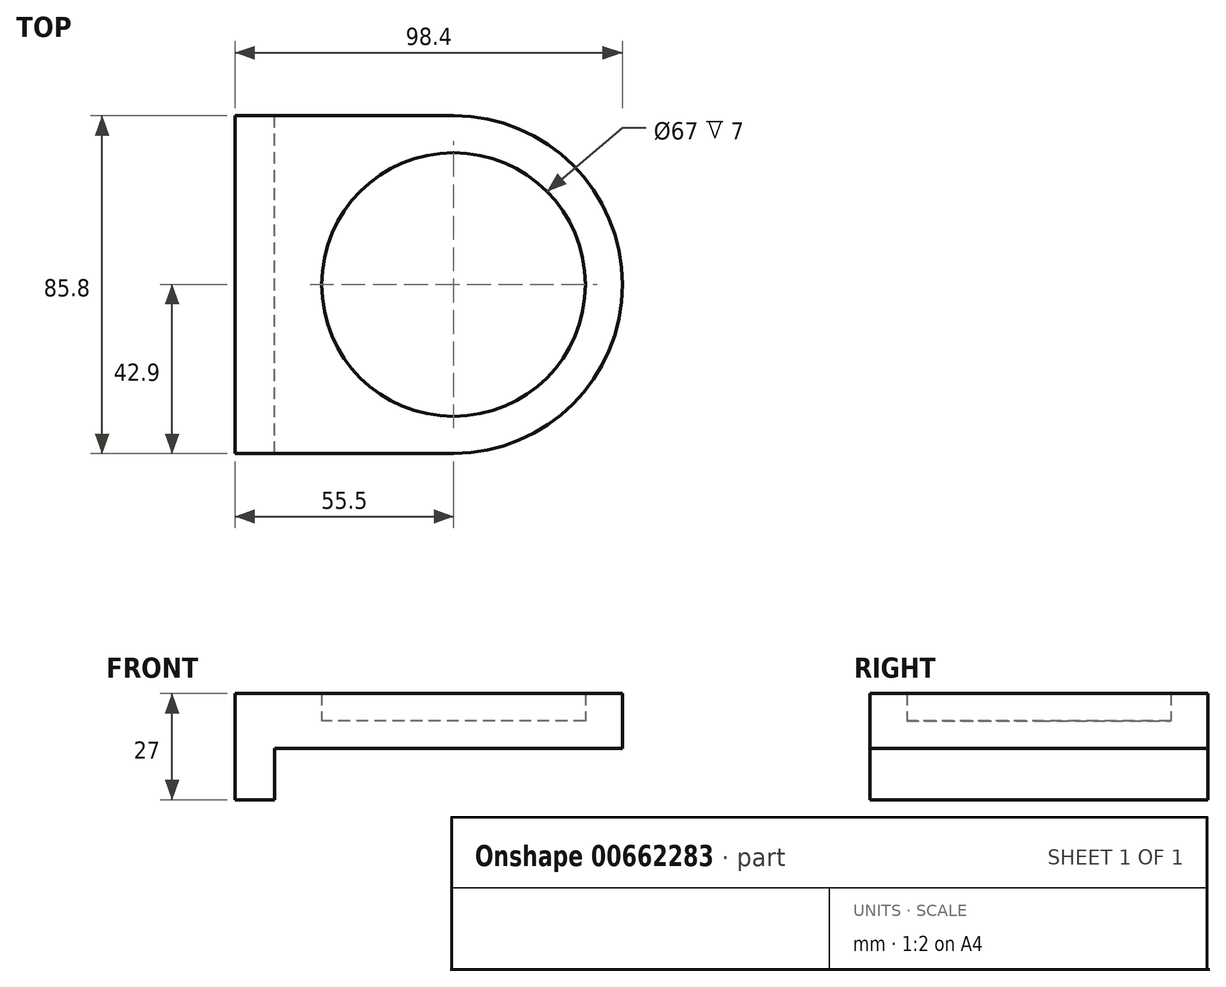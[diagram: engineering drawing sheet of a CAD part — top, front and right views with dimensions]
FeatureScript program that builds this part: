
annotation { "Feature Type Name" : "Feature", "Feature Type Description" : "" }
export const myFeature = defineFeature(function(context is Context, id is Id, definition is map)
    precondition{}
    {
        {
            var Q0;
            Q0=qCreatedBy(makeId("Top.planeOp"),FACE);
            var sketch = newSketch(context, id + "F0", { "sketchPlane" : qUnion([Q0])});
            skCircle(sketch, "E0", {"center": v(0, 0) * mm, "radius": 33.5 * mm});
            skCircle(sketch, "E1", {"center": v(0, 0) * mm, "radius": 42.9 * mm});
            skLineSegment(sketch, "E2", {"start": v(0, 42.9) * mm, "end": v(-55.5, 42.9) * mm});
            skLineSegment(sketch, "E3", {"start": v(-55.5, -42.9) * mm, "end": v(0, -42.9) * mm});
            skLineSegment(sketch, "E4", {"start": v(-55.5, 42.9) * mm, "end": v(-55.5, -42.9) * mm});
            skSolve(sketch);
        }
        {
            var Q0;
            {var subQ0=sQuery(id+"F0.wireOp",EDGE,"E3");Q0=makeQuery(id+"F0.imprint","IMPRINT",FACE,{"disambiguationData":[TD([[makeQuery(id+"F0.imprint","IMPRINT",EDGE,{"derivedFrom":subQ0}),1.0]])]});}
            var Q1;
            {var subQ0=sQuery(id+"F0.wireOp",EDGE,"E2");Q1=makeQuery(id+"F0.imprint","IMPRINT",FACE,{"disambiguationData":[TD([[makeQuery(id+"F0.imprint","IMPRINT",EDGE,{"derivedFrom":subQ0}),1.0]])]});}
            var Q2;
            Q2=makeQuery(id+"F0.imprint","IMPRINT",FACE,{"disambiguationData":[TD([[makeQuery(id+"F0.imprint","IMPRINT",EDGE,{"derivedFrom":sQuery(id+"F0.wireOp",EDGE,"E0")}),-1.0]])]});
            extrude(context, id + "F1", {"entities" : qUnion([Q0, Q1, Q2]), "depth" : 7 * mm, "offsetDistance" : 25.4 * mm});
        }
        {
            var Q0;
            Q0=makeQuery(id+"F1.opExtrude","CAP_FACE",FACE,{"disambiguationData":[OSD([sQuery(id+"F0.wireOp",EDGE,"E0"),sQuery(id+"F0.wireOp",EDGE,"E1"),sQuery(id+"F0.wireOp",EDGE,"E2"),sQuery(id+"F0.wireOp",EDGE,"B6yvLt6C-i46t-O52Y-Rehz-RWSLDy2yBdGn"),sQuery(id+"F0.wireOp",EDGE,"E3")])],"isStart":true});
            var sketch = newSketch(context, id + "F2", { "sketchPlane" : qUnion([Q0])});
            skArc(sketch, "E5", {"start": v(0, -42.9) * mm, "mid": v(42.9, 0) * mm, "end": v(0, 42.9) * mm});
            skLineSegment(sketch, "E6", {"start": v(-55.5, 42.9) * mm, "end": v(0, 42.9) * mm});
            skLineSegment(sketch, "E7", {"start": v(0, -42.9) * mm, "end": v(0, -42.9) * mm});
            skLineSegment(sketch, "E8", {"start": v(-55.5, 42.9) * mm, "end": v(-55.5, -42.9) * mm});
            skLineSegment(sketch, "E9", {"start": v(-55.5, -42.9) * mm, "end": v(0, -42.9) * mm});
            skSolve(sketch);
        }
        {
            var Q0;
            Q0 = qSketchRegion(id + "F2", true);
            extrude(context, id + "F3", {"entities" : qUnion([Q0]), "operationType" : NewBodyOperationType.ADD, "depth" : 7 * mm, "offsetDistance" : 25.4 * mm});
        }
        {
            var Q0;
            Q0=makeQuery(id+"F3.opExtrude","CAP_FACE",FACE,{"disambiguationData":[OSD([sQuery(id+"F2.wireOp",EDGE,"E5"),sQuery(id+"F2.wireOp",EDGE,"E6"),sQuery(id+"F2.wireOp",EDGE,"E8"),sQuery(id+"F2.wireOp",EDGE,"E9")])],"isStart":false});
            var sketch = newSketch(context, id + "F4", { "sketchPlane" : qUnion([Q0])});
            skLineSegment(sketch, "E10.bottom", {"start": v(-55.5, 42.9) * mm, "end": v(-45.5, 42.9) * mm});
            skLineSegment(sketch, "E10.top", {"start": v(-55.5, -42.9) * mm, "end": v(-45.5, -42.9) * mm});
            skLineSegment(sketch, "E10.left", {"start": v(-55.5, 42.9) * mm, "end": v(-55.5, -42.9) * mm});
            skLineSegment(sketch, "E10.right", {"start": v(-45.5, 42.9) * mm, "end": v(-45.5, -42.9) * mm});
            skSolve(sketch);
        }
        {
            var Q0;
            Q0=makeQuery(id+"F4.imprint","IMPRINT",FACE,{"disambiguationData":[TD([[makeQuery(id+"F4.imprint","IMPRINT",EDGE,{"derivedFrom":sQuery(id+"F4.wireOp",EDGE,"E10.bottom")}),-1.0]])]});
            extrude(context, id + "F5", {"entities" : qUnion([Q0]), "operationType" : NewBodyOperationType.ADD, "depth" : 13 * mm, "offsetDistance" : 25.4 * mm});
        }
    });
